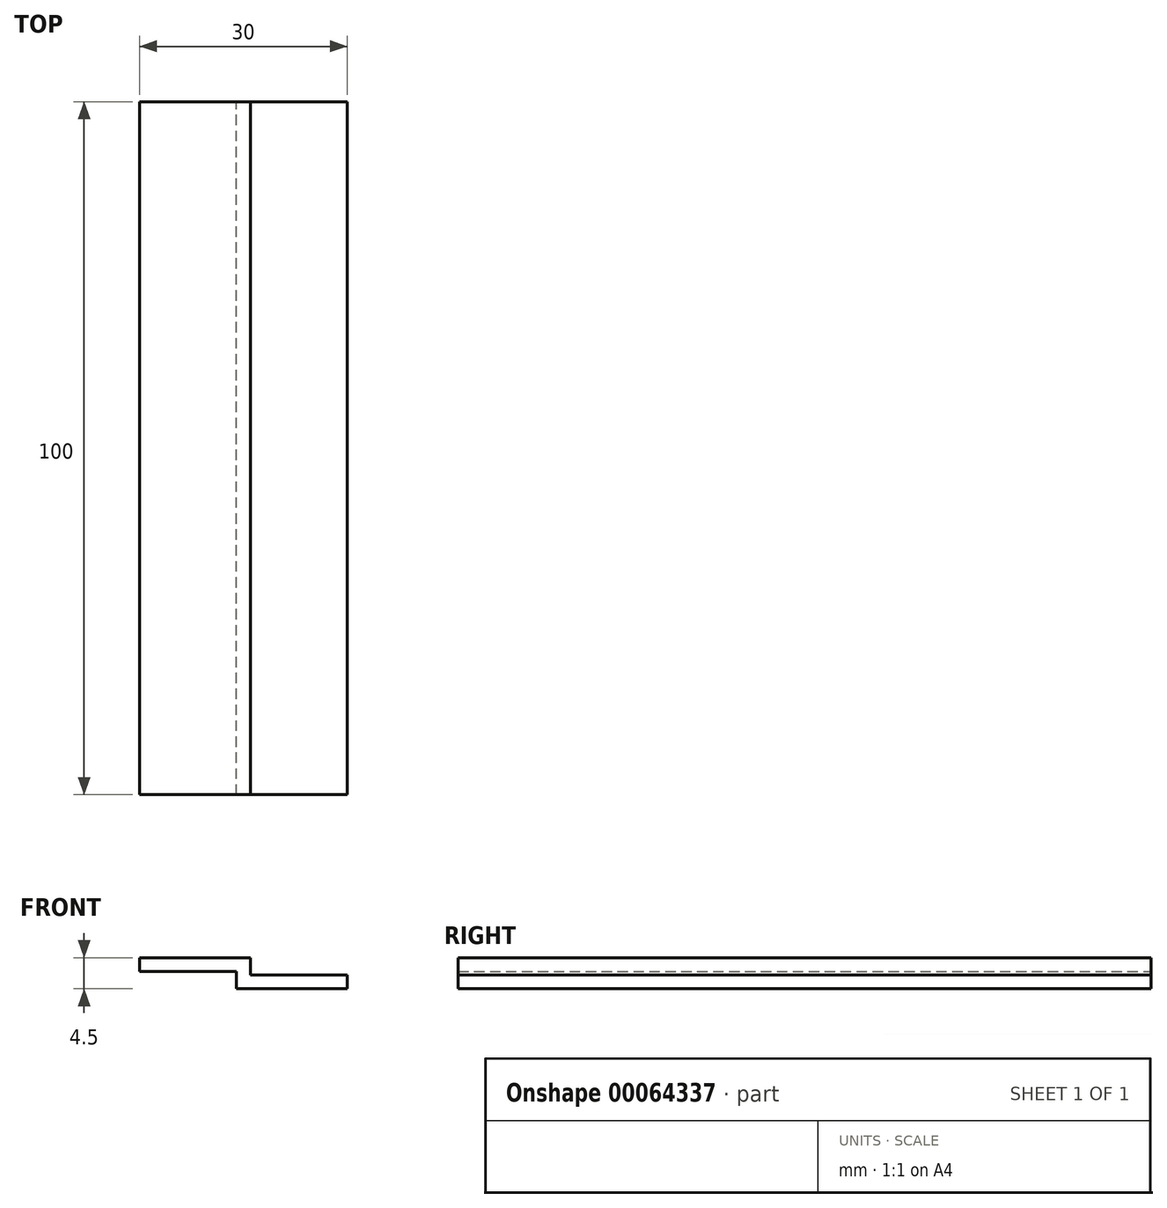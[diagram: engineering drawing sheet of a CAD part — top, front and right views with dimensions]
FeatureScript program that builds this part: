
annotation { "Feature Type Name" : "Feature", "Feature Type Description" : "" }
export const myFeature = defineFeature(function(context is Context, id is Id, definition is map)
    precondition{}
    {
        {
            var Q0;
            Q0=qCreatedBy(makeId("Front.planeOp"),FACE);
            var sketch = newSketch(context, id + "F0", { "sketchPlane" : qUnion([Q0])});
            skLineSegment(sketch, "E0", {"start": v(0, 0) * mm, "end": v(16, 0) * mm});
            skLineSegment(sketch, "E1", {"start": v(16, 0) * mm, "end": v(16, -2.5) * mm});
            skLineSegment(sketch, "E2", {"start": v(16, -2.5) * mm, "end": v(30, -2.5) * mm});
            skLineSegment(sketch, "E3", {"start": v(30, -2.5) * mm, "end": v(30, -4.5) * mm});
            skLineSegment(sketch, "E4", {"start": v(30, -4.5) * mm, "end": v(14, -4.5) * mm});
            skLineSegment(sketch, "E5", {"start": v(14, -4.5) * mm, "end": v(14, -2) * mm});
            skLineSegment(sketch, "E6", {"start": v(14, -2) * mm, "end": v(0, -2) * mm});
            skLineSegment(sketch, "E7", {"start": v(0, -2) * mm, "end": v(0, 0) * mm});
            skSolve(sketch);
        }
        {
            var Q0;
            Q0=makeQuery(id+"F0.imprint","IMPRINT",FACE,{"disambiguationData":[TD([[makeQuery(id+"F0.imprint","IMPRINT",EDGE,{"derivedFrom":sQuery(id+"F0.wireOp",EDGE,"E0")}),-1.0]])]});
            extrude(context, id + "F1", {"entities" : qUnion([Q0]), "depth" : 100 * mm});
        }
    });
